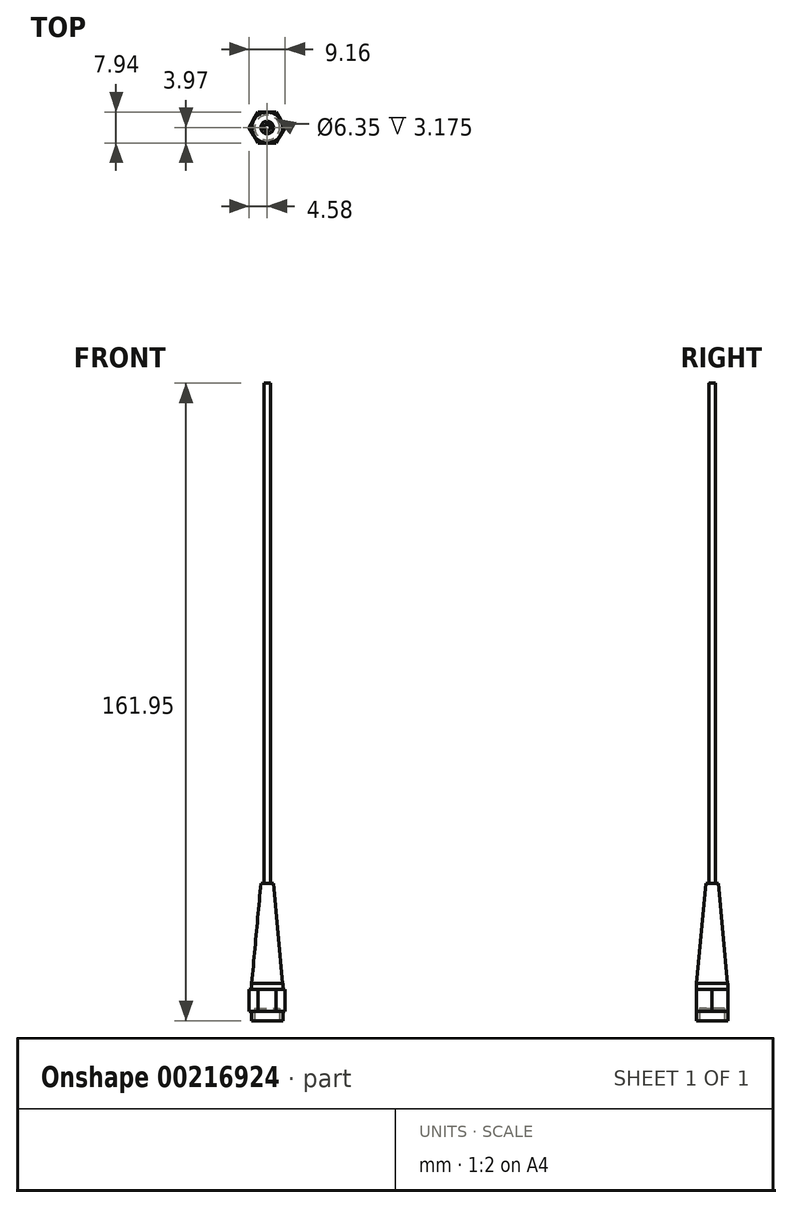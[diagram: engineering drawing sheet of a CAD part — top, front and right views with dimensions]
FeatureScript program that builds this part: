
annotation { "Feature Type Name" : "Feature", "Feature Type Description" : "" }
export const myFeature = defineFeature(function(context is Context, id is Id, definition is map)
    precondition{}
    {
        {
            var Q0;
            Q0=qCreatedBy(makeId("Top.planeOp"),FACE);
            var sketch = newSketch(context, id + "F0", { "sketchPlane" : qUnion([Q0])});
            skCircle(sketch, "E0", {"center": v(0, 0) * mm, "radius": 3.97 * mm});
            skSolve(sketch);
        }
        {
            var Q0;
            Q0 = qSketchRegion(id + "F0", true);
            extrude(context, id + "F1", {"entities" : qUnion([Q0]), "depth" : 2.38 * mm});
        }
        {
            var Q0;
            Q0=makeQuery(id+"F1.opExtrude","CAP_FACE",FACE,{"disambiguationData":[OSD([sQuery(id+"F0.wireOp",EDGE,"E0")])],"isStart":false});
            var sketch = newSketch(context, id + "F2", { "sketchPlane" : qUnion([Q0])});
            skCircle(sketch, "E1.cCircle", {"center": v(0, 0) * mm, "radius": 3.97 * mm, "construction": true});
            skLineSegment(sketch, "E1.0", {"start": v(-2.3, 3.97) * mm, "end": v(2.3, 3.97) * mm});
            skLineSegment(sketch, "E1.1", {"start": v(2.3, 3.97) * mm, "end": v(4.58, 0) * mm});
            skLineSegment(sketch, "E1.2", {"start": v(4.58, 0) * mm, "end": v(2.3, -3.97) * mm});
            skLineSegment(sketch, "E1.3", {"start": v(2.3, -3.97) * mm, "end": v(-2.3, -3.97) * mm});
            skLineSegment(sketch, "E1.4", {"start": v(-2.3, -3.97) * mm, "end": v(-4.58, 0) * mm});
            skLineSegment(sketch, "E1.5", {"start": v(-4.58, 0) * mm, "end": v(-2.3, 3.97) * mm});
            skPoint(sketch, "E1.0.midPoint", {"position": v(0, 3.97) * mm});
            skSolve(sketch);
        }
        {
            var Q0;
            Q0 = qSketchRegion(id + "F2", true);
            extrude(context, id + "F3", {"entities" : qUnion([Q0]), "operationType" : NewBodyOperationType.ADD, "depth" : 5.56 * mm});
        }
        {
            var Q0;
            Q0=makeQuery(id+"F3.opExtrude","CAP_FACE",FACE,{"disambiguationData":[OSD([sQuery(id+"F2.wireOp",EDGE,"E1.0"),sQuery(id+"F2.wireOp",EDGE,"E1.1"),sQuery(id+"F2.wireOp",EDGE,"E1.2"),sQuery(id+"F2.wireOp",EDGE,"E1.3"),sQuery(id+"F2.wireOp",EDGE,"E1.4"),sQuery(id+"F2.wireOp",EDGE,"E1.5")])],"isStart":false});
            var sketch = newSketch(context, id + "F4", { "sketchPlane" : qUnion([Q0])});
            skCircle(sketch, "E2", {"center": v(0, 0) * mm, "radius": 3.97 * mm});
            skSolve(sketch);
        }
        {
            var Q0;
            Q0 = qSketchRegion(id + "F4", true);
            extrude(context, id + "F5", {"entities" : qUnion([Q0]), "operationType" : NewBodyOperationType.ADD, "depth" : 1.59 * mm});
        }
        {
            var Q0;
            Q0=makeQuery(id+"F1.opExtrude","CAP_FACE",FACE,{"disambiguationData":[OSD([sQuery(id+"F0.wireOp",EDGE,"E0")])],"isStart":true});
            var sketch = newSketch(context, id + "F6", { "sketchPlane" : qUnion([Q0])});
            skCircle(sketch, "E3", {"center": v(0, 0) * mm, "radius": 3.18 * mm});
            skSolve(sketch);
        }
        {
            var Q0;
            Q0 = qSketchRegion(id + "F6", true);
            extrude(context, id + "F7", {"entities" : qUnion([Q0]), "operationType" : NewBodyOperationType.REMOVE, "oppositeDirection" : true, "depth" : 3.17 * mm});
        }
        {
            var Q0;
            Q0=makeQuery(id+"F5.opExtrude","CAP_FACE",FACE,{"disambiguationData":[OSD([sQuery(id+"F4.wireOp",EDGE,"E2")])],"isStart":false});
            var sketch = newSketch(context, id + "F8", { "sketchPlane" : qUnion([Q0])});
            skCircle(sketch, "E4", {"center": v(0, 0) * mm, "radius": 3.77 * mm, "construction": true});
            skCircle(sketch, "E5", {"center": v(0, 0) * mm, "radius": 1.59 * mm});
            skSolve(sketch);
        }
        {
            var Q0;
            Q0 = qSketchRegion(id + "F8", true);
            extrude(context, id + "F9", {"entities" : qUnion([Q0]), "operationType" : NewBodyOperationType.ADD, "depth" : 25.4 * mm});
        }
        {
            var Q0;
            Q0=qCreatedBy(makeId("Front.planeOp"),FACE);
            var sketch = newSketch(context, id + "F10", { "sketchPlane" : qUnion([Q0])});
            skLineSegment(sketch, "E6", {"start": v(0, 34.93) * mm, "end": v(1.59, 34.93) * mm});
            skLineSegment(sketch, "E7", {"start": v(1.59, 34.93) * mm, "end": v(3.92, 9.53) * mm});
            skLineSegment(sketch, "E8", {"start": v(3.92, 9.53) * mm, "end": v(0, 9.53) * mm});
            skLineSegment(sketch, "E9", {"start": v(0, 9.53) * mm, "end": v(0, 34.93) * mm});
            skSolve(sketch);
        }
        {
            var Q0;
            Q0 = qSketchRegion(id + "F10", true);
            var Q1;
            Q1=makeQuery(id+"F5.opExtrude","CAP_EDGE",EDGE,{"disambiguationData":[OSD([sQuery(id+"F4.wireOp",EDGE,"E2")])],"isStart":false});
            revolve(context, id + "F11", {"operationType" : NewBodyOperationType.ADD, "entities" : qUnion([Q0]), "axis" : qUnion([Q1]), "revolveType" : RevolveType.FULL});
        }
        {
            var Q0;
            Q0=makeQuery(id+"F9.opExtrude","CAP_FACE",FACE,{"disambiguationData":[OSD([sQuery(id+"F8.wireOp",EDGE,"E5")])],"isStart":false});
            var sketch = newSketch(context, id + "F12", { "sketchPlane" : qUnion([Q0])});
            skCircle(sketch, "E10", {"center": v(0, 0) * mm, "radius": 0.8 * mm});
            skSolve(sketch);
        }
        {
            var Q0;
            Q0 = qSketchRegion(id + "F12", true);
            extrude(context, id + "F13", {"entities" : qUnion([Q0]), "operationType" : NewBodyOperationType.ADD, "depth" : 127 * mm + 11 / 406.4 * mm});
        }
    });
